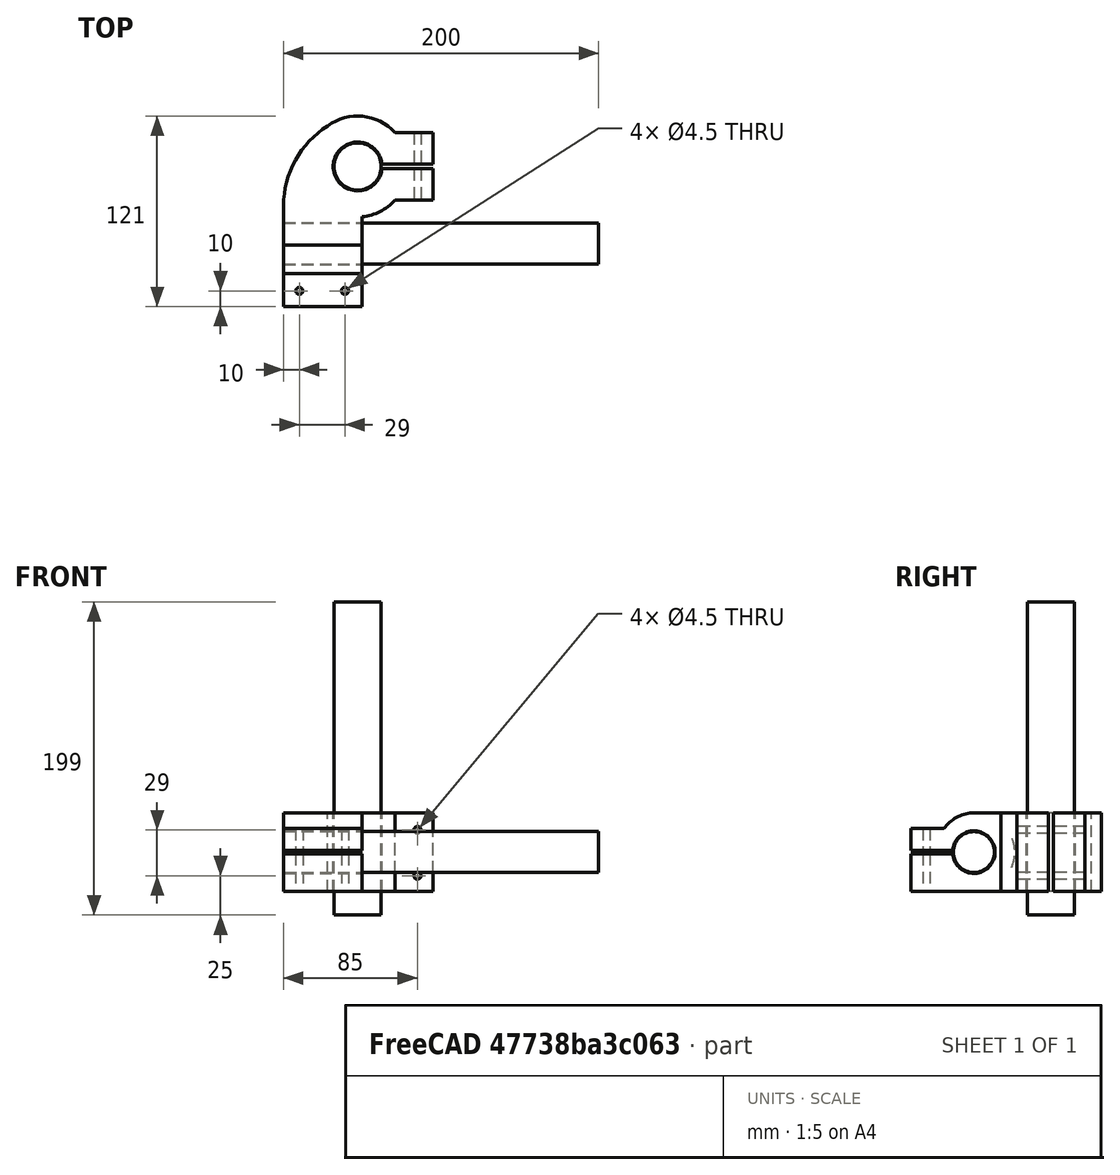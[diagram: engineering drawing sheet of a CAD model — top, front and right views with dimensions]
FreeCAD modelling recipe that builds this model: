
FCSTD DOCUMENT  (FreeCAD 0.19R24276 (Git))
Label: camMountFront2022_02_26
License: All rights reserved
LicenseURL: http://en.wikipedia.org/wiki/All_rights_reserved
objects: Part::Cylinder×9, Part::Box×8, Part::MultiFuse×4, Part::FeaturePython×2, Part::Cut×1
note: 24 computed .brp shape members not serialized (recipe doc carries the construction recipe); baked Part::Feature solids carry a one-line shape summary decoded from their .brp

FEATURE [Part::Cylinder] Cylinder  label="Horizontal"
  Angle = 360
  AttacherType = Attacher::AttachEngine3D
  Height = 199
  Radius = 15
FEATURE [Part::Cylinder] Cylinder001  label="Vertical"
  Angle = 360
  AttacherType = Attacher::AttachEngine3D
  Height = 200
  Placement = pos=(-47,-49,40) rot=(0.57735,0.57735,0.57735;2.0944rad)
  Radius = 13
FEATURE [Part::FeaturePython] Tube  label="TubeAddons"  # WARN: FeaturePython — macro-defined, semantics opaque (R4)
  AttacherType = Attacher::AttachEngine3D
  Height = 50
  InnerRadius = 15.5
  OuterRadius = 32
  Placement = pos=(0,0,15) rot=(0,0,1;0rad)
FEATURE [Part::FeaturePython] Tube001  label="TubeAddons001"  # WARN: FeaturePython — macro-defined, semantics opaque (R4)
  AttacherType = Attacher::AttachEngine3D
  Height = 50
  InnerRadius = 13.5
  OuterRadius = 25
  Placement = pos=(-47,-48,40) rot=(0,1,0;1.5708rad)
FEATURE [Part::Box] Box  label="horCuts"
  AttacherType = Attacher::AttachEngine3D
  Height = 50
  Length = 20
  Placement = pos=(14,-1.5,15) rot=(0,0,1;0rad)
  Width = 3
FEATURE [Part::Box] Box001  label="horAdd"
  AttacherType = Attacher::AttachEngine3D
  Height = 50
  Length = 25
  Placement = pos=(23,-21.5,15) rot=(0,0,1;0rad)
  Width = 20
FEATURE [Part::Box] Box002  label="horAdd001"
  AttacherType = Attacher::AttachEngine3D
  Height = 50
  Length = 25
  Placement = pos=(23,1.5,15) rot=(0,0,1;0rad)
  Width = 20
FEATURE [Part::Box] Box003  label="VerAddons"
  AttacherType = Attacher::AttachEngine3D
  Height = 10
  Length = 50
  Placement = pos=(-47,-89,15) rot=(0,0,1;0rad)
  Width = 63
FEATURE [Part::Box] Box004  label="VerAddons001"
  AttacherType = Attacher::AttachEngine3D
  Height = 14
  Length = 50
  Placement = pos=(-47,-89,25) rot=(0,0,1;0rad)
  Width = 25
FEATURE [Part::Box] Box005  label="VerAddons002"
  AttacherType = Attacher::AttachEngine3D
  Height = 14
  Length = 50
  Placement = pos=(-47,-89,41) rot=(0,0,1;0rad)
  Width = 24
FEATURE [Part::Box] Box006  label="verCuts"
  AttacherType = Attacher::AttachEngine3D
  Height = 2
  Length = 50
  Placement = pos=(-47,-89,39) rot=(0,0,1;0rad)
  Width = 27
FEATURE [Part::Cylinder] Cylinder002  label="AddCylinder"
  Angle = 60
  AttacherType = Attacher::AttachEngine3D
  Height = 50
  Placement = pos=(13,-25,15) rot=(0,0,1;2.0944rad)
  Radius = 60
FEATURE [Part::Box] Box007  label="VerAddons003"
  AttacherType = Attacher::AttachEngine3D
  Height = 50
  Length = 50
  Placement = pos=(-47,-50,15) rot=(0,0,1;0rad)
  Width = 25
FEATURE [Part::Cylinder] Cylinder003  label="Vertical001Cuts"
  Angle = 360
  AttacherType = Attacher::AttachEngine3D
  Height = 200
  Placement = pos=(-47,-49,40) rot=(0.57735,0.57735,0.57735;2.0944rad)
  Radius = 13.5
FEATURE [Part::Cylinder] Cylinder004  label="Horizontal001Cuts"
  Angle = 360
  AttacherType = Attacher::AttachEngine3D
  Height = 199
  Radius = 15.5
FEATURE [Part::Cylinder] Cylinder005  label="m4s"
  Angle = 360
  AttacherType = Attacher::AttachEngine3D
  Height = 50
  Placement = pos=(38,22,25) rot=(1,0,0;1.5708rad)
  Radius = 2.25
FEATURE [Part::Cylinder] Cylinder006  label="m4s001"
  Angle = 360
  AttacherType = Attacher::AttachEngine3D
  Height = 50
  Placement = pos=(38,22,54) rot=(1,0,0;1.5708rad)
  Radius = 2.25
FEATURE [Part::MultiFuse] Fusion  label="m4s002"
  Placement = pos=(-62,-117,43) rot=(0.57735,0.57735,0.57735;2.0944rad)
  Shapes = -> [Cylinder006,Cylinder005]
FEATURE [Part::Cylinder] Cylinder007  label="m4s004"
  Angle = 360
  AttacherType = Attacher::AttachEngine3D
  Height = 50
  Placement = pos=(38,22,25) rot=(1,0,0;1.5708rad)
  Radius = 2.25
FEATURE [Part::Cylinder] Cylinder008  label="m4s005"
  Angle = 360
  AttacherType = Attacher::AttachEngine3D
  Height = 50
  Placement = pos=(38,22,54) rot=(1,0,0;1.5708rad)
  Radius = 2.25
FEATURE [Part::MultiFuse] Fusion001  label="m4s003"
  Shapes = -> [Cylinder008,Cylinder007]
FEATURE [Part::MultiFuse] Fusion002  label="cuts"
  Shapes = -> [Box,Fusion,Fusion001,Cylinder004,Cylinder003,Box006]
FEATURE [Part::MultiFuse] Fusion003  label="Adds"
  Shapes = -> [Box007,Cylinder002,Box005,Box004,Box003,Box002,Box001,Tube001,Tube]
FEATURE [Part::Cut] Cut  label="left"
  Base = -> Fusion003
  Tool = -> Fusion002
